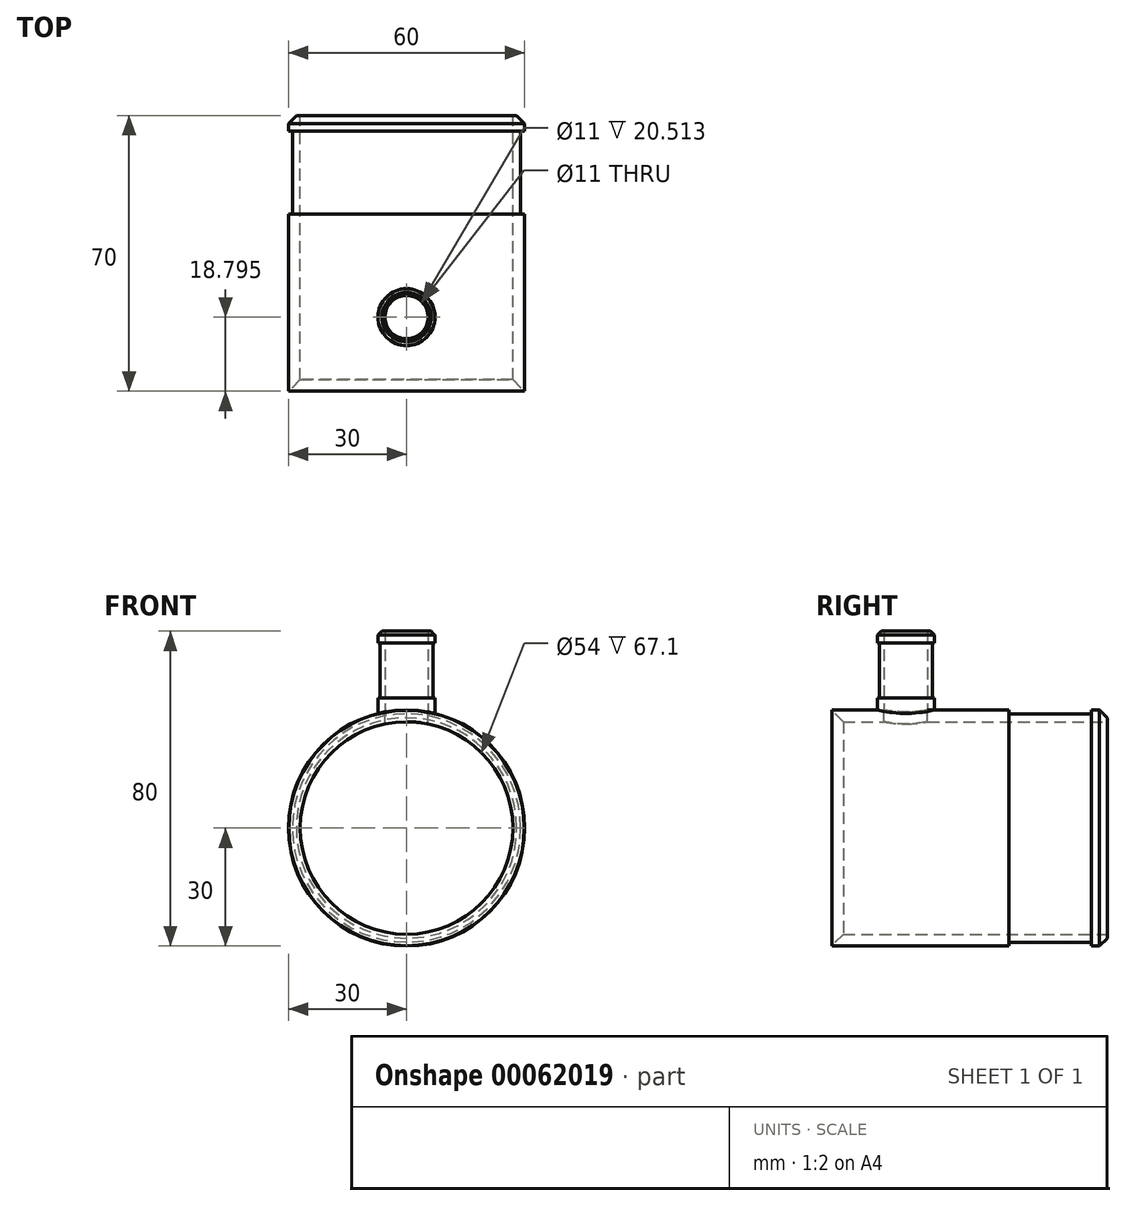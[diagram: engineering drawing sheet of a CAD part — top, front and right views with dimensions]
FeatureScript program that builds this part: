
annotation { "Feature Type Name" : "Feature", "Feature Type Description" : "" }
export const myFeature = defineFeature(function(context is Context, id is Id, definition is map)
    precondition{}
    {
        {
            var Q0;
            Q0=qCreatedBy(makeId("Right.planeOp"),FACE);
            var sketch = newSketch(context, id + "F0", { "sketchPlane" : qUnion([Q0])});
            skLineSegment(sketch, "E0", {"start": v(0, 0) * mm, "end": v(-70, 0) * mm, "construction": true});
            skLineSegment(sketch, "E1", {"start": v(-70, 27) * mm, "end": v(-70, 30) * mm});
            skLineSegment(sketch, "E2", {"start": v(-70, 30) * mm, "end": v(-25, 30) * mm});
            skLineSegment(sketch, "E3", {"start": v(-25, 30) * mm, "end": v(-25, 29) * mm});
            skLineSegment(sketch, "E4", {"start": v(-25, 29) * mm, "end": v(-4, 29) * mm});
            skLineSegment(sketch, "E5", {"start": v(-4, 29) * mm, "end": v(-4, 30) * mm});
            skLineSegment(sketch, "E6", {"start": v(-4, 30) * mm, "end": v(-2, 30) * mm});
            skLineSegment(sketch, "E7", {"start": v(-2, 30) * mm, "end": v(0, 28) * mm});
            skLineSegment(sketch, "E8", {"start": v(0, 28) * mm, "end": v(0, 27) * mm});
            skLineSegment(sketch, "E9", {"start": v(-70, 27) * mm, "end": v(0, 27) * mm});
            skSolve(sketch);
        }
        {
            var Q0;
            Q0=makeQuery(id+"F0.imprint","IMPRINT",FACE,{"disambiguationData":[TD([[makeQuery(id+"F0.imprint","IMPRINT",EDGE,{"derivedFrom":sQuery(id+"F0.wireOp",EDGE,"E1")}),-1.0]])]});
            var Q1;
            Q1=sQuery(id+"F0.wireOp",EDGE,"E0");
            revolve(context, id + "F1", {"entities" : qUnion([Q0]), "axis" : qUnion([Q1]), "revolveType" : RevolveType.FULL});
        }
        {
            var Q0;
            Q0=qCreatedBy(makeId("Top.planeOp"),FACE);
            var sketch = newSketch(context, id + "F2", { "sketchPlane" : qUnion([Q0])});
            skCircle(sketch, "E10", {"center": v(0, -51.2) * mm, "radius": 7.25 * mm});
            skCircle(sketch, "E11", {"center": v(0, -51.2) * mm, "radius": 5.5 * mm});
            skSolve(sketch);
        }
        {
            var Q0;
            Q0 = qSketchRegion(id + "F2", true);
            var Q1;
            Q1=makeQuery(id+"F1.opRevolve","SWEPT_FACE",FACE,{"disambiguationData":[OSD([sQuery(id+"F0.wireOp",EDGE,"E2")])]});
            extrude(context, id + "F3", {"entities" : qUnion([Q0]), "depth" : 50 * mm, "hasSecondDirection" : true, "secondDirectionBound" : BoundingType.UP_TO_SURFACE, "secondDirectionOppositeDirection" : false, "secondDirectionBoundEntityFace" : qUnion([Q1]), "secondDirectionDepth" : 25 * mm});
        }
        {
            var Q0;
            {var subQ0=sQuery(id+"F2.wireOp",EDGE,"E10");var subQ1=sQuery(id+"F2.wireOp",EDGE,"E11");Q0=makeQuery(id+"F3.opExtrude","CAP_FACE",FACE,{"disambiguationData":[OSD([subQ0,subQ1]),topologyDisambiguationEdgeConnected([makeQuery(id+"F2.imprint","IMPRINT",EDGE,{"derivedFrom":subQ0})])],"isStart":false});}
            var sketch = newSketch(context, id + "F4", { "sketchPlane" : qUnion([Q0])});
            skCircle(sketch, "E12.0", {"center": v(0, -51.2) * mm, "radius": 5.5 * mm});
            skSolve(sketch);
        }
        {
            var Q0;
            Q0 = qSketchRegion(id + "F4", true);
            var Q1;
            Q1=makeQuery(id+"F1.opRevolve","SWEPT_FACE",FACE,{"disambiguationData":[OSD([sQuery(id+"F0.wireOp",EDGE,"E9")])]});
            extrude(context, id + "F5", {"entities" : qUnion([Q0]), "operationType" : NewBodyOperationType.REMOVE, "endBound" : BoundingType.UP_TO_SURFACE, "oppositeDirection" : true, "endBoundEntityFace" : qUnion([Q1]), "depth" : 25 * mm});
        }
        {
            var Q0;
            {var subQ0=sQuery(id+"F2.wireOp",EDGE,"E10");var subQ1=sQuery(id+"F2.wireOp",EDGE,"E11");Q0=makeQuery(id+"F3.opExtrude","CAP_FACE",FACE,{"disambiguationData":[OSD([subQ0,subQ1]),topologyDisambiguationEdgeConnected([makeQuery(id+"F2.imprint","IMPRINT",EDGE,{"derivedFrom":subQ0})])],"isStart":false});}
            var sketch = newSketch(context, id + "F6", { "sketchPlane" : qUnion([Q0])});
            skCircle(sketch, "E13.0", {"center": v(0, -51.2) * mm, "radius": 7.25 * mm, "construction": true});
            skCircle(sketch, "E14.0", {"center": v(0, -51.2) * mm, "radius": 7.75 * mm});
            skCircle(sketch, "E15.0", {"center": v(0, -51.2) * mm, "radius": 6.75 * mm});
            skSolve(sketch);
        }
        {
            var Q0;
            Q0 = qSketchRegion(id + "F6", true);
            extrude(context, id + "F7", {"entities" : qUnion([Q0]), "operationType" : NewBodyOperationType.REMOVE, "oppositeDirection" : true, "depth" : 17 * mm, "hasSecondDirection" : true, "secondDirectionOppositeDirection" : true, "secondDirectionDepth" : 3 * mm});
        }
        {
            var Q0;
            {var subQ0=sQuery(id+"F2.wireOp",EDGE,"E10");Q0=makeQuery(id+"F3.opExtrude","CAP_EDGE",EDGE,{"disambiguationData":[OSD([subQ0]),topologyDisambiguationEdgeConnected([makeQuery(id+"F2.imprint","IMPRINT",EDGE,{"derivedFrom":subQ0})])],"isStart":false});}
            chamfer(context, id + "F8", {"entities" : qUnion([Q0]), "width" : 1 * mm, "tangentPropagation" : true});
        }
        {
            var Q0;
            Q0=makeQuery(id+"F1.opRevolve","SWEPT_EDGE",EDGE,{"disambiguationData":[OSD([sQuery(id+"F0.wireOp",EDGE,"E1"),sQuery(id+"F0.wireOp",EDGE,"E9")])]});
            chamfer(context, id + "F9", {"entities" : qUnion([Q0]), "width" : 2.9 * mm, "tangentPropagation" : true});
        }
    });
